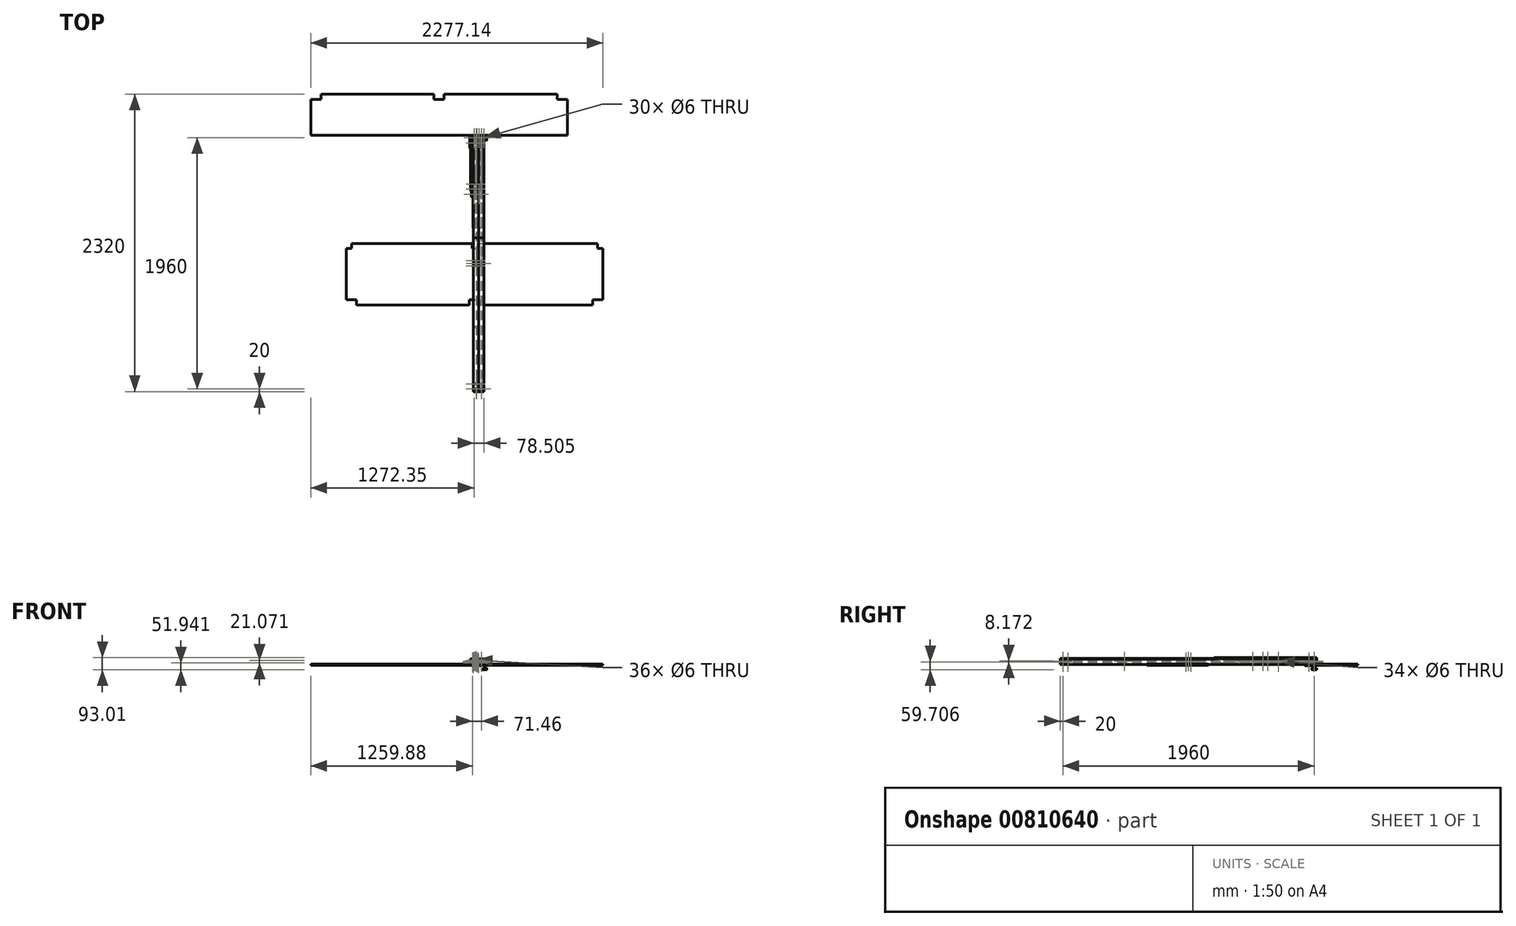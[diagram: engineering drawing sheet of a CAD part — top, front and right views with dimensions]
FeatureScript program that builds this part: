
annotation { "Feature Type Name" : "Feature", "Feature Type Description" : "" }
export const myFeature = defineFeature(function(context is Context, id is Id, definition is map)
    precondition{}
    {
        {
            var Q0;
            Q0=qCreatedBy(makeId("Front.planeOp"),FACE);
            var sketch = newSketch(context, id + "F0", { "sketchPlane" : qUnion([Q0])});
            skLineSegment(sketch, "E0.bottom", {"start": v(-48.85, 47.04) * mm, "end": v(31.15, 47.04) * mm});
            skLineSegment(sketch, "E0.top", {"start": v(-48.85, 7.04) * mm, "end": v(31.15, 7.04) * mm});
            skLineSegment(sketch, "E0.left", {"start": v(-48.85, 47.04) * mm, "end": v(-48.85, 7.04) * mm});
            skLineSegment(sketch, "E0.right", {"start": v(31.15, 47.04) * mm, "end": v(31.15, 7.04) * mm});
            skSolve(sketch);
        }
        {
            var Q0;
            Q0=makeQuery(id+"F0.imprint","IMPRINT",FACE,{"disambiguationData":[TD([[makeQuery(id+"F0.imprint","IMPRINT",EDGE,{"derivedFrom":sQuery(id+"F0.wireOp",EDGE,"E0.bottom")}),-1.0]])]});
            extrude(context, id + "F1", {"entities" : qUnion([Q0]), "depth" : 2000 * mm, "offsetDistance" : 25 * mm});
        }
        {
            var Q0;
            Q0=makeQuery(id+"F1.opExtrude","CAP_FACE",FACE,{"disambiguationData":[OSD([sQuery(id+"F0.wireOp",EDGE,"E0.bottom"),sQuery(id+"F0.wireOp",EDGE,"E0.top"),sQuery(id+"F0.wireOp",EDGE,"E0.left"),sQuery(id+"F0.wireOp",EDGE,"E0.right")])],"isStart":false});
            var sketch = newSketch(context, id + "F2", { "sketchPlane" : qUnion([Q0])});
            skPoint(sketch, "E1", {"position": v(-28.85, 27.04) * mm});
            skPoint(sketch, "E2", {"position": v(11.15, 27.04) * mm});
            skSolve(sketch);
        }
        {
            var Q0;
            Q0=makeQuery(id+"F1.opExtrude","SWEPT_EDGE",EDGE,{"disambiguationData":[OSD([sQuery(id+"F0.wireOp",EDGE,"E0.bottom"),sQuery(id+"F0.wireOp",EDGE,"E0.left")])]});
            var Q1;
            Q1=makeQuery(id+"F1.opExtrude","SWEPT_EDGE",EDGE,{"disambiguationData":[OSD([sQuery(id+"F0.wireOp",EDGE,"E0.bottom"),sQuery(id+"F0.wireOp",EDGE,"E0.right")])]});
            var Q2;
            Q2=makeQuery(id+"F1.opExtrude","SWEPT_EDGE",EDGE,{"disambiguationData":[OSD([sQuery(id+"F0.wireOp",EDGE,"E0.top"),sQuery(id+"F0.wireOp",EDGE,"E0.right")])]});
            var Q3;
            Q3=makeQuery(id+"F1.opExtrude","SWEPT_EDGE",EDGE,{"disambiguationData":[OSD([sQuery(id+"F0.wireOp",EDGE,"E0.top"),sQuery(id+"F0.wireOp",EDGE,"E0.left")])]});
            fillet(context, id + "F3", {"entities" : qUnion([Q0, Q1, Q2, Q3]), "radius" : 5 * mm, "tangentPropagation" : true, "allowEdgeOverflow" : false});
        }
        {
            var Q0;
            Q0=makeQuery(id+"F1.opExtrude","SWEPT_FACE",FACE,{"disambiguationData":[OSD([sQuery(id+"F0.wireOp",EDGE,"E0.left")])]});
            var sketch = newSketch(context, id + "F4", { "sketchPlane" : qUnion([Q0])});
            skPoint(sketch, "E3", {"position": v(20, 27.04) * mm});
            skPoint(sketch, "E4", {"position": v(60, 27.04) * mm});
            skPoint(sketch, "E5", {"position": v(1000, 27.04) * mm});
            skPoint(sketch, "E6", {"position": v(1020, 27.04) * mm});
            skPoint(sketch, "E7", {"position": v(980, 27.04) * mm});
            skPoint(sketch, "E8", {"position": v(1980, 27.04) * mm});
            skPoint(sketch, "E9", {"position": v(1940, 27.04) * mm});
            skSolve(sketch);
        }
        {
            var Q0;
            Q0=makeQuery(id+"F1.opExtrude","SWEPT_FACE",FACE,{"disambiguationData":[OSD([sQuery(id+"F0.wireOp",EDGE,"E0.top")])]});
            var sketch = newSketch(context, id + "F5", { "sketchPlane" : qUnion([Q0])});
            skPoint(sketch, "E10", {"position": v(-28.85, 1980) * mm});
            skPoint(sketch, "E11", {"position": v(11.15, 1980) * mm});
            skPoint(sketch, "E12", {"position": v(-28.85, 1000) * mm});
            skPoint(sketch, "E12.positionSnap0", {"position": v(-43.85, 1000) * mm});
            skPoint(sketch, "E13", {"position": v(11.15, 1000) * mm});
            skPoint(sketch, "E14", {"position": v(-28.85, 20) * mm});
            skPoint(sketch, "E15", {"position": v(11.15, 20) * mm});
            skSolve(sketch);
        }
        {
            var Q0;
            Q0=sQuery(id+"F5.wireOp",VERTEX,"E15");
            var Q1;
            Q1=sQuery(id+"F5.wireOp",VERTEX,"E14");
            var Q2;
            Q2=sQuery(id+"F4.wireOp",VERTEX,"E3");
            var Q3;
            Q3=sQuery(id+"F4.wireOp",VERTEX,"E4");
            var Q4;
            Q4=sQuery(id+"F4.wireOp",VERTEX,"E6");
            var Q5;
            Q5=sQuery(id+"F4.wireOp",VERTEX,"E7");
            var Q6;
            Q6=sQuery(id+"F5.wireOp",VERTEX,"E12");
            var Q7;
            Q7=sQuery(id+"F5.wireOp",VERTEX,"E13");
            var Q8;
            Q8=sQuery(id+"F4.wireOp",VERTEX,"E9");
            var Q9;
            Q9=sQuery(id+"F4.wireOp",VERTEX,"E8");
            var Q10;
            Q10=sQuery(id+"F5.wireOp",VERTEX,"E10");
            var Q11;
            Q11=sQuery(id+"F5.wireOp",VERTEX,"E11");
            var Q12;
            Q12=sQuery(id+"F2.wireOp",VERTEX,"E1");
            var Q13;
            Q13=sQuery(id+"F2.wireOp",VERTEX,"E2");
            var Q14;
            Q14=makeQuery(id+"F1.opExtrude","SWEPT_BODY",BODY,{"disambiguationData":[OSD([sQuery(id+"F0.wireOp",EDGE,"E0.bottom"),sQuery(id+"F0.wireOp",EDGE,"E0.top"),sQuery(id+"F0.wireOp",EDGE,"E0.left"),sQuery(id+"F0.wireOp",EDGE,"E0.right")])]});
            hole(context, id + "F6", {"style" : HoleStyle.SIMPLE, "endStyle" : HoleEndStyle.THROUGH, "holeDiameter" : 6 * mm, "majorDiameter" : 5 * mm, "isTappedThrough" : true, "tappedDepth" : 12 * mm, "tapClearance" : 3, "locations" : qUnion([Q0, Q1, Q2, Q3, Q4, Q5, Q6, Q7, Q8, Q9, Q10, Q11, Q12, Q13]), "scope" : qUnion([Q14])});
        }
        {
            var Q0;
            Q0=qCreatedBy(makeId("Front.planeOp"),FACE);
            var sketch = newSketch(context, id + "F7", { "sketchPlane" : qUnion([Q0])});
            skLineSegment(sketch, "E16.bottom", {"start": v(-49.88, 49.92) * mm, "end": v(30.12, 49.92) * mm});
            skLineSegment(sketch, "E16.top", {"start": v(-49.88, 9.08) * mm, "end": v(30.12, 9.08) * mm});
            skLineSegment(sketch, "E16.left", {"start": v(-49.88, 49.92) * mm, "end": v(-49.88, 9.08) * mm});
            skLineSegment(sketch, "E16.right", {"start": v(30.12, 49.92) * mm, "end": v(30.12, 9.08) * mm});
            skSolve(sketch);
        }
        {
            var Q0;
            Q0=makeQuery(id+"F7.imprint","IMPRINT",FACE,{"disambiguationData":[TD([[makeQuery(id+"F7.imprint","IMPRINT",EDGE,{"derivedFrom":sQuery(id+"F7.wireOp",EDGE,"E16.bottom")}),-1.0]])]});
            extrude(context, id + "F8", {"entities" : qUnion([Q0]), "depth" : 720 * mm, "offsetDistance" : 25 * mm});
        }
        {
            var Q0;
            Q0=makeQuery(id+"F8.opExtrude","CAP_FACE",FACE,{"disambiguationData":[OSD([sQuery(id+"F7.wireOp",EDGE,"E16.bottom"),sQuery(id+"F7.wireOp",EDGE,"E16.top"),sQuery(id+"F7.wireOp",EDGE,"E16.left"),sQuery(id+"F7.wireOp",EDGE,"E16.right")])],"isStart":false});
            var sketch = newSketch(context, id + "F9", { "sketchPlane" : qUnion([Q0])});
            skPoint(sketch, "E17", {"position": v(-29.88, 29.92) * mm});
            skPoint(sketch, "E18", {"position": v(10.12, 29.92) * mm});
            skSolve(sketch);
        }
        {
            var Q0;
            Q0=makeQuery(id+"F8.opExtrude","SWEPT_EDGE",EDGE,{"disambiguationData":[OSD([sQuery(id+"F7.wireOp",EDGE,"E16.bottom"),sQuery(id+"F7.wireOp",EDGE,"E16.left")])]});
            var Q1;
            Q1=makeQuery(id+"F8.opExtrude","SWEPT_EDGE",EDGE,{"disambiguationData":[OSD([sQuery(id+"F7.wireOp",EDGE,"E16.bottom"),sQuery(id+"F7.wireOp",EDGE,"E16.right")])]});
            var Q2;
            Q2=makeQuery(id+"F8.opExtrude","SWEPT_EDGE",EDGE,{"disambiguationData":[OSD([sQuery(id+"F7.wireOp",EDGE,"E16.top"),sQuery(id+"F7.wireOp",EDGE,"E16.right")])]});
            var Q3;
            Q3=makeQuery(id+"F8.opExtrude","SWEPT_EDGE",EDGE,{"disambiguationData":[OSD([sQuery(id+"F7.wireOp",EDGE,"E16.top"),sQuery(id+"F7.wireOp",EDGE,"E16.left")])]});
            fillet(context, id + "F10", {"entities" : qUnion([Q0, Q1, Q2, Q3]), "radius" : 5 * mm, "tangentPropagation" : true, "allowEdgeOverflow" : false});
        }
        {
            var Q0;
            Q0=sQuery(id+"F9.wireOp",VERTEX,"E17");
            var Q1;
            Q1=sQuery(id+"F9.wireOp",VERTEX,"E18");
            var Q2;
            Q2=makeQuery(id+"F8.opExtrude","SWEPT_BODY",BODY,{"disambiguationData":[OSD([sQuery(id+"F7.wireOp",EDGE,"E16.bottom"),sQuery(id+"F7.wireOp",EDGE,"E16.top"),sQuery(id+"F7.wireOp",EDGE,"E16.left"),sQuery(id+"F7.wireOp",EDGE,"E16.right")])]});
            hole(context, id + "F11", {"style" : HoleStyle.SIMPLE, "endStyle" : HoleEndStyle.THROUGH, "holeDiameter" : 6 * mm, "majorDiameter" : 5 * mm, "isTappedThrough" : true, "tappedDepth" : 12 * mm, "tapClearance" : 3, "locations" : qUnion([Q0, Q1]), "scope" : qUnion([Q2])});
        }
        {
            var Q0;
            Q0=qCreatedBy(makeId("Front.planeOp"),FACE);
            var sketch = newSketch(context, id + "F12", { "sketchPlane" : qUnion([Q0])});
            skLineSegment(sketch, "E19.bottom", {"start": v(-50.66, 52.94) * mm, "end": v(29.34, 52.94) * mm});
            skLineSegment(sketch, "E19.top", {"start": v(-50.66, 12.94) * mm, "end": v(29.34, 12.94) * mm});
            skLineSegment(sketch, "E19.left", {"start": v(-50.66, 52.94) * mm, "end": v(-50.66, 12.94) * mm});
            skLineSegment(sketch, "E19.right", {"start": v(29.34, 52.94) * mm, "end": v(29.34, 12.94) * mm});
            skSolve(sketch);
        }
        {
            var Q0;
            Q0=makeQuery(id+"F12.imprint","IMPRINT",FACE,{"disambiguationData":[TD([[makeQuery(id+"F12.imprint","IMPRINT",EDGE,{"derivedFrom":sQuery(id+"F12.wireOp",EDGE,"E19.bottom")}),-1.0]])]});
            extrude(context, id + "F13", {"entities" : qUnion([Q0]), "depth" : 800 * mm, "offsetDistance" : 25 * mm});
        }
        {
            var Q0;
            Q0=makeQuery(id+"F13.opExtrude","SWEPT_EDGE",EDGE,{"disambiguationData":[OSD([sQuery(id+"F12.wireOp",EDGE,"E19.bottom"),sQuery(id+"F12.wireOp",EDGE,"E19.left")])]});
            var Q1;
            Q1=makeQuery(id+"F13.opExtrude","SWEPT_EDGE",EDGE,{"disambiguationData":[OSD([sQuery(id+"F12.wireOp",EDGE,"E19.bottom"),sQuery(id+"F12.wireOp",EDGE,"E19.right")])]});
            var Q2;
            Q2=makeQuery(id+"F13.opExtrude","SWEPT_EDGE",EDGE,{"disambiguationData":[OSD([sQuery(id+"F12.wireOp",EDGE,"E19.top"),sQuery(id+"F12.wireOp",EDGE,"E19.left")])]});
            var Q3;
            Q3=makeQuery(id+"F13.opExtrude","SWEPT_EDGE",EDGE,{"disambiguationData":[OSD([sQuery(id+"F12.wireOp",EDGE,"E19.top"),sQuery(id+"F12.wireOp",EDGE,"E19.right")])]});
            fillet(context, id + "F14", {"entities" : qUnion([Q0, Q1, Q2, Q3]), "radius" : 5 * mm, "tangentPropagation" : true, "allowEdgeOverflow" : false});
        }
        {
            var Q0;
            Q0=makeQuery(id+"F13.opExtrude","CAP_FACE",FACE,{"disambiguationData":[OSD([sQuery(id+"F12.wireOp",EDGE,"E19.bottom"),sQuery(id+"F12.wireOp",EDGE,"E19.top"),sQuery(id+"F12.wireOp",EDGE,"E19.left"),sQuery(id+"F12.wireOp",EDGE,"E19.right")])],"isStart":false});
            var sketch = newSketch(context, id + "F15", { "sketchPlane" : qUnion([Q0])});
            skPoint(sketch, "E20", {"position": v(-30.66, 32.94) * mm});
            skPoint(sketch, "E20.positionSnap0", {"position": v(-50.66, 32.94) * mm});
            skPoint(sketch, "E21", {"position": v(9.34, 32.94) * mm});
            skSolve(sketch);
        }
        {
            var Q0;
            Q0=makeQuery(id+"F13.opExtrude","SWEPT_FACE",FACE,{"disambiguationData":[OSD([sQuery(id+"F12.wireOp",EDGE,"E19.left")])]});
            var sketch = newSketch(context, id + "F16", { "sketchPlane" : qUnion([Q0])});
            skPoint(sketch, "E22", {"position": v(400, 32.94) * mm});
            skPoint(sketch, "E23", {"position": v(420, 32.94) * mm});
            skPoint(sketch, "E24", {"position": v(380, 32.94) * mm});
            skSolve(sketch);
        }
        {
            var Q0;
            Q0=sQuery(id+"F16.wireOp",VERTEX,"E24");
            var Q1;
            Q1=sQuery(id+"F16.wireOp",VERTEX,"E23");
            var Q2;
            Q2=sQuery(id+"F15.wireOp",VERTEX,"E20");
            var Q3;
            Q3=sQuery(id+"F15.wireOp",VERTEX,"E21");
            var Q4;
            Q4=makeQuery(id+"F13.opExtrude","SWEPT_BODY",BODY,{"disambiguationData":[OSD([sQuery(id+"F12.wireOp",EDGE,"E19.bottom"),sQuery(id+"F12.wireOp",EDGE,"E19.top"),sQuery(id+"F12.wireOp",EDGE,"E19.left"),sQuery(id+"F12.wireOp",EDGE,"E19.right")])]});
            hole(context, id + "F17", {"style" : HoleStyle.SIMPLE, "endStyle" : HoleEndStyle.THROUGH, "holeDiameter" : 6 * mm, "majorDiameter" : 5 * mm, "isTappedThrough" : true, "tappedDepth" : 12 * mm, "tapClearance" : 3, "locations" : qUnion([Q0, Q1, Q2, Q3]), "scope" : qUnion([Q4])});
        }
        {
            var Q0;
            Q0=qCreatedBy(makeId("Front.planeOp"),FACE);
            var sketch = newSketch(context, id + "F18", { "sketchPlane" : qUnion([Q0])});
            skLineSegment(sketch, "E25.bottom", {"start": v(-51.7, 60.34) * mm, "end": v(-11.7, 60.34) * mm});
            skLineSegment(sketch, "E25.top", {"start": v(-51.7, 20.34) * mm, "end": v(-11.7, 20.34) * mm});
            skLineSegment(sketch, "E25.left", {"start": v(-51.7, 60.34) * mm, "end": v(-51.7, 20.34) * mm});
            skLineSegment(sketch, "E25.right", {"start": v(-11.7, 60.34) * mm, "end": v(-11.7, 20.34) * mm});
            skSolve(sketch);
        }
        {
            var Q0;
            Q0=makeQuery(id+"F18.imprint","IMPRINT",FACE,{"disambiguationData":[TD([[makeQuery(id+"F18.imprint","IMPRINT",EDGE,{"derivedFrom":sQuery(id+"F18.wireOp",EDGE,"E25.bottom")}),-1.0]])]});
            extrude(context, id + "F19", {"entities" : qUnion([Q0]), "depth" : 800 * mm, "offsetDistance" : 25 * mm});
        }
        {
            var Q0;
            Q0=makeQuery(id+"F19.opExtrude","SWEPT_EDGE",EDGE,{"disambiguationData":[OSD([sQuery(id+"F18.wireOp",EDGE,"E25.bottom"),sQuery(id+"F18.wireOp",EDGE,"E25.left")])]});
            var Q1;
            Q1=makeQuery(id+"F19.opExtrude","SWEPT_EDGE",EDGE,{"disambiguationData":[OSD([sQuery(id+"F18.wireOp",EDGE,"E25.bottom"),sQuery(id+"F18.wireOp",EDGE,"E25.right")])]});
            var Q2;
            Q2=makeQuery(id+"F19.opExtrude","SWEPT_EDGE",EDGE,{"disambiguationData":[OSD([sQuery(id+"F18.wireOp",EDGE,"E25.top"),sQuery(id+"F18.wireOp",EDGE,"E25.right")])]});
            var Q3;
            Q3=makeQuery(id+"F19.opExtrude","SWEPT_EDGE",EDGE,{"disambiguationData":[OSD([sQuery(id+"F18.wireOp",EDGE,"E25.top"),sQuery(id+"F18.wireOp",EDGE,"E25.left")])]});
            fillet(context, id + "F20", {"entities" : qUnion([Q0, Q1, Q2, Q3]), "radius" : 5 * mm, "tangentPropagation" : true, "allowEdgeOverflow" : false});
        }
        {
            var Q0;
            Q0=makeQuery(id+"F19.opExtrude","CAP_FACE",FACE,{"disambiguationData":[OSD([sQuery(id+"F18.wireOp",EDGE,"E25.bottom"),sQuery(id+"F18.wireOp",EDGE,"E25.top"),sQuery(id+"F18.wireOp",EDGE,"E25.left"),sQuery(id+"F18.wireOp",EDGE,"E25.right")])],"isStart":false});
            var sketch = newSketch(context, id + "F21", { "sketchPlane" : qUnion([Q0])});
            skPoint(sketch, "E26", {"position": v(-31.7, 40.34) * mm});
            skPoint(sketch, "E26.positionSnap0", {"position": v(-51.7, 40.34) * mm});
            skPoint(sketch, "E26.positionSnap1", {"position": v(-31.7, 60.34) * mm});
            skSolve(sketch);
        }
        {
            var Q0;
            Q0=makeQuery(id+"F19.opExtrude","SWEPT_FACE",FACE,{"disambiguationData":[OSD([sQuery(id+"F18.wireOp",EDGE,"E25.bottom")])]});
            var sketch = newSketch(context, id + "F22", { "sketchPlane" : qUnion([Q0])});
            skPoint(sketch, "E27", {"position": v(-31.7, -400) * mm});
            skPoint(sketch, "E28", {"position": v(-31.7, -380) * mm});
            skPoint(sketch, "E29", {"position": v(-31.7, -420) * mm});
            skSolve(sketch);
        }
        {
            var Q0;
            Q0=sQuery(id+"F22.wireOp",VERTEX,"E28");
            var Q1;
            Q1=sQuery(id+"F22.wireOp",VERTEX,"E29");
            var Q2;
            Q2=sQuery(id+"F21.wireOp",VERTEX,"E26");
            var Q3;
            Q3=makeQuery(id+"F19.opExtrude","SWEPT_BODY",BODY,{"disambiguationData":[OSD([sQuery(id+"F18.wireOp",EDGE,"E25.bottom"),sQuery(id+"F18.wireOp",EDGE,"E25.top"),sQuery(id+"F18.wireOp",EDGE,"E25.left"),sQuery(id+"F18.wireOp",EDGE,"E25.right")])]});
            hole(context, id + "F23", {"style" : HoleStyle.SIMPLE, "endStyle" : HoleEndStyle.THROUGH, "holeDiameter" : 6 * mm, "majorDiameter" : 5 * mm, "isTappedThrough" : true, "tappedDepth" : 12 * mm, "tapClearance" : 3, "locations" : qUnion([Q0, Q1, Q2]), "scope" : qUnion([Q3])});
        }
        {
            var Q0;
            Q0=qCreatedBy(makeId("Front.planeOp"),FACE);
            var sketch = newSketch(context, id + "F24", { "sketchPlane" : qUnion([Q0])});
            skLineSegment(sketch, "E30.bottom", {"start": v(-51.72, 54) * mm, "end": v(-11.72, 54) * mm});
            skLineSegment(sketch, "E30.top", {"start": v(-51.72, 14) * mm, "end": v(-11.72, 14) * mm});
            skLineSegment(sketch, "E30.left", {"start": v(-51.72, 54) * mm, "end": v(-51.72, 14) * mm});
            skLineSegment(sketch, "E30.right", {"start": v(-11.72, 54) * mm, "end": v(-11.72, 14) * mm});
            skSolve(sketch);
        }
        {
            var Q0;
            Q0=makeQuery(id+"F24.imprint","IMPRINT",FACE,{"disambiguationData":[TD([[makeQuery(id+"F24.imprint","IMPRINT",EDGE,{"derivedFrom":sQuery(id+"F24.wireOp",EDGE,"E30.bottom")}),-1.0]])]});
            extrude(context, id + "F25", {"entities" : qUnion([Q0]), "depth" : 2000 * mm, "offsetDistance" : 25 * mm});
        }
        {
            var Q0;
            Q0=makeQuery(id+"F25.opExtrude","SWEPT_EDGE",EDGE,{"disambiguationData":[OSD([sQuery(id+"F24.wireOp",EDGE,"E30.bottom"),sQuery(id+"F24.wireOp",EDGE,"E30.left")])]});
            var Q1;
            Q1=makeQuery(id+"F25.opExtrude","SWEPT_EDGE",EDGE,{"disambiguationData":[OSD([sQuery(id+"F24.wireOp",EDGE,"E30.bottom"),sQuery(id+"F24.wireOp",EDGE,"E30.right")])]});
            var Q2;
            Q2=makeQuery(id+"F25.opExtrude","SWEPT_EDGE",EDGE,{"disambiguationData":[OSD([sQuery(id+"F24.wireOp",EDGE,"E30.top"),sQuery(id+"F24.wireOp",EDGE,"E30.right")])]});
            var Q3;
            Q3=makeQuery(id+"F25.opExtrude","SWEPT_EDGE",EDGE,{"disambiguationData":[OSD([sQuery(id+"F24.wireOp",EDGE,"E30.top"),sQuery(id+"F24.wireOp",EDGE,"E30.left")])]});
            fillet(context, id + "F26", {"entities" : qUnion([Q0, Q1, Q2, Q3]), "radius" : 5 * mm, "tangentPropagation" : true, "allowEdgeOverflow" : false});
        }
        {
            var Q0;
            Q0=makeQuery(id+"F25.opExtrude","SWEPT_FACE",FACE,{"disambiguationData":[OSD([sQuery(id+"F24.wireOp",EDGE,"E30.left")])]});
            var sketch = newSketch(context, id + "F27", { "sketchPlane" : qUnion([Q0])});
            skPoint(sketch, "E31", {"position": v(20, 34) * mm});
            skPoint(sketch, "E31.positionSnap0", {"position": v(0, 34) * mm});
            skPoint(sketch, "E32", {"position": v(1000, 34) * mm});
            skPoint(sketch, "E33", {"position": v(500, 34) * mm});
            skPoint(sketch, "E34", {"position": v(1500, 34) * mm});
            skPoint(sketch, "E35", {"position": v(1980, 34) * mm});
            skSolve(sketch);
        }
        {
            var Q0;
            Q0=makeQuery(id+"F25.opExtrude","SWEPT_FACE",FACE,{"disambiguationData":[OSD([sQuery(id+"F24.wireOp",EDGE,"E30.bottom")])]});
            var sketch = newSketch(context, id + "F28", { "sketchPlane" : qUnion([Q0])});
            skPoint(sketch, "E36", {"position": v(-31.72, -1980) * mm});
            skPoint(sketch, "E36.positionSnap0", {"position": v(-31.72, -2000) * mm});
            skPoint(sketch, "E37", {"position": v(-31.72, -1940) * mm});
            skPoint(sketch, "E38", {"position": v(-31.72, -1000) * mm});
            skPoint(sketch, "E39", {"position": v(-31.72, -1020) * mm});
            skPoint(sketch, "E40", {"position": v(-31.72, -980) * mm});
            skPoint(sketch, "E41", {"position": v(-31.72, -20) * mm});
            skPoint(sketch, "E42", {"position": v(-31.72, -60) * mm});
            skSolve(sketch);
        }
        {
            var Q0;
            Q0=sQuery(id+"F28.wireOp",VERTEX,"E36");
            var Q1;
            Q1=sQuery(id+"F28.wireOp",VERTEX,"E37");
            var Q2;
            Q2=sQuery(id+"F28.wireOp",VERTEX,"E39");
            var Q3;
            Q3=sQuery(id+"F28.wireOp",VERTEX,"E40");
            var Q4;
            Q4=sQuery(id+"F27.wireOp",VERTEX,"E34");
            var Q5;
            Q5=sQuery(id+"F27.wireOp",VERTEX,"E35");
            var Q6;
            Q6=sQuery(id+"F27.wireOp",VERTEX,"E32");
            var Q7;
            Q7=sQuery(id+"F27.wireOp",VERTEX,"E33");
            var Q8;
            Q8=sQuery(id+"F28.wireOp",VERTEX,"E42");
            var Q9;
            Q9=sQuery(id+"F28.wireOp",VERTEX,"E41");
            var Q10;
            Q10=sQuery(id+"F27.wireOp",VERTEX,"E31");
            var Q11;
            Q11=makeQuery(id+"F25.opExtrude","SWEPT_BODY",BODY,{"disambiguationData":[OSD([sQuery(id+"F24.wireOp",EDGE,"E30.bottom"),sQuery(id+"F24.wireOp",EDGE,"E30.top"),sQuery(id+"F24.wireOp",EDGE,"E30.left"),sQuery(id+"F24.wireOp",EDGE,"E30.right")])]});
            hole(context, id + "F29", {"style" : HoleStyle.SIMPLE, "endStyle" : HoleEndStyle.THROUGH, "holeDiameter" : 6 * mm, "majorDiameter" : 5 * mm, "isTappedThrough" : true, "tappedDepth" : 12 * mm, "tapClearance" : 3, "locations" : qUnion([Q0, Q1, Q2, Q3, Q4, Q5, Q6, Q7, Q8, Q9, Q10]), "scope" : qUnion([Q11])});
        }
        {
            var Q0;
            Q0=qCreatedBy(makeId("Front.planeOp"),FACE);
            var sketch = newSketch(context, id + "F30", { "sketchPlane" : qUnion([Q0])});
            skLineSegment(sketch, "E43.bottom", {"start": v(-55.62, 55.2) * mm, "end": v(-15.62, 55.2) * mm});
            skLineSegment(sketch, "E43.top", {"start": v(-55.62, 15.2) * mm, "end": v(-15.62, 15.2) * mm});
            skLineSegment(sketch, "E43.left", {"start": v(-55.62, 55.2) * mm, "end": v(-55.62, 15.2) * mm});
            skLineSegment(sketch, "E43.right", {"start": v(-15.62, 55.2) * mm, "end": v(-15.62, 15.2) * mm});
            skSolve(sketch);
        }
        {
            var Q0;
            Q0=makeQuery(id+"F30.imprint","IMPRINT",FACE,{"disambiguationData":[TD([[makeQuery(id+"F30.imprint","IMPRINT",EDGE,{"derivedFrom":sQuery(id+"F30.wireOp",EDGE,"E43.bottom")}),-1.0]])]});
            extrude(context, id + "F31", {"entities" : qUnion([Q0]), "depth" : 720 * mm, "offsetDistance" : 25 * mm});
        }
        {
            var Q0;
            Q0=makeQuery(id+"F31.opExtrude","SWEPT_EDGE",EDGE,{"disambiguationData":[OSD([sQuery(id+"F30.wireOp",EDGE,"E43.bottom"),sQuery(id+"F30.wireOp",EDGE,"E43.left")])]});
            var Q1;
            Q1=makeQuery(id+"F31.opExtrude","SWEPT_EDGE",EDGE,{"disambiguationData":[OSD([sQuery(id+"F30.wireOp",EDGE,"E43.bottom"),sQuery(id+"F30.wireOp",EDGE,"E43.right")])]});
            var Q2;
            Q2=makeQuery(id+"F31.opExtrude","SWEPT_EDGE",EDGE,{"disambiguationData":[OSD([sQuery(id+"F30.wireOp",EDGE,"E43.top"),sQuery(id+"F30.wireOp",EDGE,"E43.right")])]});
            var Q3;
            Q3=makeQuery(id+"F31.opExtrude","SWEPT_EDGE",EDGE,{"disambiguationData":[OSD([sQuery(id+"F30.wireOp",EDGE,"E43.top"),sQuery(id+"F30.wireOp",EDGE,"E43.left")])]});
            fillet(context, id + "F32", {"entities" : qUnion([Q0, Q1, Q2, Q3]), "radius" : 5 * mm, "tangentPropagation" : true, "allowEdgeOverflow" : false});
        }
        {
            var Q0;
            Q0=makeQuery(id+"F31.opExtrude","CAP_FACE",FACE,{"disambiguationData":[OSD([sQuery(id+"F30.wireOp",EDGE,"E43.bottom"),sQuery(id+"F30.wireOp",EDGE,"E43.top"),sQuery(id+"F30.wireOp",EDGE,"E43.left"),sQuery(id+"F30.wireOp",EDGE,"E43.right")])],"isStart":false});
            var sketch = newSketch(context, id + "F33", { "sketchPlane" : qUnion([Q0])});
            skPoint(sketch, "E44", {"position": v(-35.62, 35.2) * mm});
            skPoint(sketch, "E44.positionSnap0", {"position": v(-55.62, 35.2) * mm});
            skPoint(sketch, "E44.positionSnap1", {"position": v(-35.62, 55.2) * mm});
            skSolve(sketch);
        }
        {
            var Q0;
            Q0=sQuery(id+"F33.wireOp",VERTEX,"E44");
            var Q1;
            Q1=makeQuery(id+"F31.opExtrude","SWEPT_BODY",BODY,{"disambiguationData":[OSD([sQuery(id+"F30.wireOp",EDGE,"E43.bottom"),sQuery(id+"F30.wireOp",EDGE,"E43.top"),sQuery(id+"F30.wireOp",EDGE,"E43.left"),sQuery(id+"F30.wireOp",EDGE,"E43.right")])]});
            hole(context, id + "F34", {"style" : HoleStyle.SIMPLE, "endStyle" : HoleEndStyle.THROUGH, "holeDiameter" : 6 * mm, "majorDiameter" : 5 * mm, "isTappedThrough" : true, "tappedDepth" : 12 * mm, "tapClearance" : 3, "locations" : qUnion([Q0]), "scope" : qUnion([Q1])});
        }
        {
            var Q0;
            Q0=makeQuery(id+"F8.opExtrude","SWEPT_FACE",FACE,{"disambiguationData":[OSD([sQuery(id+"F7.wireOp",EDGE,"E16.right")])]});
            var sketch = newSketch(context, id + "F35", { "sketchPlane" : qUnion([Q0])});
            skPoint(sketch, "E45", {"position": v(-300, 29.08) * mm});
            skSolve(sketch);
        }
        {
            var Q0;
            Q0=sQuery(id+"F35.wireOp",VERTEX,"E45");
            var Q1;
            Q1=makeQuery(id+"F8.opExtrude","SWEPT_BODY",BODY,{"disambiguationData":[OSD([sQuery(id+"F7.wireOp",EDGE,"E16.bottom"),sQuery(id+"F7.wireOp",EDGE,"E16.top"),sQuery(id+"F7.wireOp",EDGE,"E16.left"),sQuery(id+"F7.wireOp",EDGE,"E16.right")])]});
            hole(context, id + "F36", {"style" : HoleStyle.SIMPLE, "endStyle" : HoleEndStyle.THROUGH, "holeDiameter" : 6 * mm, "majorDiameter" : 5 * mm, "isTappedThrough" : true, "tappedDepth" : 12 * mm, "tapClearance" : 3, "locations" : qUnion([Q0]), "scope" : qUnion([Q1])});
        }
        {
            var Q0;
            Q0=makeQuery(id+"F31.opExtrude","SWEPT_FACE",FACE,{"disambiguationData":[OSD([sQuery(id+"F30.wireOp",EDGE,"E43.right")])]});
            var sketch = newSketch(context, id + "F37", { "sketchPlane" : qUnion([Q0])});
            skPoint(sketch, "E46", {"position": v(-300, 35.2) * mm});
            skSolve(sketch);
        }
        {
            var Q0;
            Q0=sQuery(id+"F37.wireOp",VERTEX,"E46");
            var Q1;
            Q1=makeQuery(id+"F31.opExtrude","SWEPT_BODY",BODY,{"disambiguationData":[OSD([sQuery(id+"F30.wireOp",EDGE,"E43.bottom"),sQuery(id+"F30.wireOp",EDGE,"E43.top"),sQuery(id+"F30.wireOp",EDGE,"E43.left"),sQuery(id+"F30.wireOp",EDGE,"E43.right")])]});
            hole(context, id + "F38", {"style" : HoleStyle.SIMPLE, "endStyle" : HoleEndStyle.THROUGH, "holeDiameter" : 6 * mm, "majorDiameter" : 5 * mm, "isTappedThrough" : true, "tappedDepth" : 12 * mm, "tapClearance" : 3, "locations" : qUnion([Q0]), "scope" : qUnion([Q1])});
        }
        {
            var Q0;
            Q0=qCreatedBy(makeId("Front.planeOp"),FACE);
            var sketch = newSketch(context, id + "F39", { "sketchPlane" : qUnion([Q0])});
            skLineSegment(sketch, "E47.bottom", {"start": v(-80.31, 44.3) * mm, "end": v(-0.31, 44.3) * mm});
            skLineSegment(sketch, "E47.top", {"start": v(-80.31, 4.3) * mm, "end": v(-0.31, 4.3) * mm});
            skLineSegment(sketch, "E47.left", {"start": v(-80.31, 44.3) * mm, "end": v(-80.31, 4.3) * mm});
            skLineSegment(sketch, "E47.right", {"start": v(-0.31, 44.3) * mm, "end": v(-0.31, 4.3) * mm});
            skSolve(sketch);
        }
        {
            var Q0;
            Q0=makeQuery(id+"F39.imprint","IMPRINT",FACE,{"disambiguationData":[TD([[makeQuery(id+"F39.imprint","IMPRINT",EDGE,{"derivedFrom":sQuery(id+"F39.wireOp",EDGE,"E47.bottom")}),-1.0]])]});
            extrude(context, id + "F40", {"entities" : qUnion([Q0]), "depth" : 100 * mm, "offsetDistance" : 25 * mm});
        }
        {
            var Q0;
            Q0=makeQuery(id+"F40.opExtrude","SWEPT_EDGE",EDGE,{"disambiguationData":[OSD([sQuery(id+"F39.wireOp",EDGE,"E47.bottom"),sQuery(id+"F39.wireOp",EDGE,"E47.left")])]});
            var Q1;
            Q1=makeQuery(id+"F40.opExtrude","SWEPT_EDGE",EDGE,{"disambiguationData":[OSD([sQuery(id+"F39.wireOp",EDGE,"E47.top"),sQuery(id+"F39.wireOp",EDGE,"E47.left")])]});
            var Q2;
            Q2=makeQuery(id+"F40.opExtrude","SWEPT_EDGE",EDGE,{"disambiguationData":[OSD([sQuery(id+"F39.wireOp",EDGE,"E47.bottom"),sQuery(id+"F39.wireOp",EDGE,"E47.right")])]});
            var Q3;
            Q3=makeQuery(id+"F40.opExtrude","SWEPT_EDGE",EDGE,{"disambiguationData":[OSD([sQuery(id+"F39.wireOp",EDGE,"E47.top"),sQuery(id+"F39.wireOp",EDGE,"E47.right")])]});
            fillet(context, id + "F41", {"entities" : qUnion([Q0, Q1, Q2, Q3]), "radius" : 5 * mm, "tangentPropagation" : true, "allowEdgeOverflow" : false});
        }
        {
            var Q0;
            Q0=makeQuery(id+"F40.opExtrude","CAP_FACE",FACE,{"disambiguationData":[OSD([sQuery(id+"F39.wireOp",EDGE,"E47.bottom"),sQuery(id+"F39.wireOp",EDGE,"E47.top"),sQuery(id+"F39.wireOp",EDGE,"E47.left"),sQuery(id+"F39.wireOp",EDGE,"E47.right")])],"isStart":false});
            var sketch = newSketch(context, id + "F42", { "sketchPlane" : qUnion([Q0])});
            skPoint(sketch, "E48", {"position": v(-60.31, 24.3) * mm});
            skPoint(sketch, "E48.positionSnap0", {"position": v(-80.31, 24.3) * mm});
            skPoint(sketch, "E49", {"position": v(-20.31, 24.3) * mm});
            skSolve(sketch);
        }
        {
            var Q0;
            Q0=sQuery(id+"F42.wireOp",VERTEX,"E48");
            var Q1;
            Q1=sQuery(id+"F42.wireOp",VERTEX,"E49");
            var Q2;
            Q2=makeQuery(id+"F40.opExtrude","SWEPT_BODY",BODY,{"disambiguationData":[OSD([sQuery(id+"F39.wireOp",EDGE,"E47.bottom"),sQuery(id+"F39.wireOp",EDGE,"E47.top"),sQuery(id+"F39.wireOp",EDGE,"E47.left"),sQuery(id+"F39.wireOp",EDGE,"E47.right")])]});
            hole(context, id + "F43", {"style" : HoleStyle.SIMPLE, "endStyle" : HoleEndStyle.THROUGH, "holeDiameter" : 6 * mm, "majorDiameter" : 5 * mm, "isTappedThrough" : true, "tappedDepth" : 12 * mm, "tapClearance" : 3, "locations" : qUnion([Q0, Q1]), "scope" : qUnion([Q2])});
        }
        {
            var Q0;
            Q0=qCreatedBy(makeId("Front.planeOp"),FACE);
            var sketch = newSketch(context, id + "F44", { "sketchPlane" : qUnion([Q0])});
            skLineSegment(sketch, "E50.bottom", {"start": v(-67.84, 51.91) * mm, "end": v(12.16, 51.91) * mm});
            skLineSegment(sketch, "E50.top", {"start": v(-67.84, 11.91) * mm, "end": v(12.16, 11.91) * mm});
            skLineSegment(sketch, "E50.left", {"start": v(-67.84, 51.91) * mm, "end": v(-67.84, 11.91) * mm});
            skLineSegment(sketch, "E50.right", {"start": v(12.16, 51.91) * mm, "end": v(12.16, 11.91) * mm});
            skSolve(sketch);
        }
        {
            var Q0;
            Q0=makeQuery(id+"F44.imprint","IMPRINT",FACE,{"disambiguationData":[TD([[makeQuery(id+"F44.imprint","IMPRINT",EDGE,{"derivedFrom":sQuery(id+"F44.wireOp",EDGE,"E50.bottom")}),-1.0]])]});
            extrude(context, id + "F45", {"entities" : qUnion([Q0]), "depth" : 480 * mm, "offsetDistance" : 25 * mm});
        }
        {
            var Q0;
            Q0=makeQuery(id+"F45.opExtrude","SWEPT_EDGE",EDGE,{"disambiguationData":[OSD([sQuery(id+"F44.wireOp",EDGE,"E50.bottom"),sQuery(id+"F44.wireOp",EDGE,"E50.left")])]});
            var Q1;
            Q1=makeQuery(id+"F45.opExtrude","SWEPT_EDGE",EDGE,{"disambiguationData":[OSD([sQuery(id+"F44.wireOp",EDGE,"E50.bottom"),sQuery(id+"F44.wireOp",EDGE,"E50.right")])]});
            var Q2;
            Q2=makeQuery(id+"F45.opExtrude","SWEPT_EDGE",EDGE,{"disambiguationData":[OSD([sQuery(id+"F44.wireOp",EDGE,"E50.top"),sQuery(id+"F44.wireOp",EDGE,"E50.right")])]});
            var Q3;
            Q3=makeQuery(id+"F45.opExtrude","SWEPT_EDGE",EDGE,{"disambiguationData":[OSD([sQuery(id+"F44.wireOp",EDGE,"E50.top"),sQuery(id+"F44.wireOp",EDGE,"E50.left")])]});
            fillet(context, id + "F46", {"entities" : qUnion([Q0, Q1, Q2, Q3]), "radius" : 5 * mm, "tangentPropagation" : true, "allowEdgeOverflow" : false});
        }
        {
            var Q0;
            Q0=makeQuery(id+"F45.opExtrude","SWEPT_FACE",FACE,{"disambiguationData":[OSD([sQuery(id+"F44.wireOp",EDGE,"E50.bottom")])]});
            var sketch = newSketch(context, id + "F47", { "sketchPlane" : qUnion([Q0])});
            skPoint(sketch, "E51", {"position": v(-47.84, -20) * mm});
            skPoint(sketch, "E52", {"position": v(-7.84, -20) * mm});
            skPoint(sketch, "E53", {"position": v(-47.84, -460) * mm});
            skPoint(sketch, "E54", {"position": v(-7.84, -460) * mm});
            skSolve(sketch);
        }
        {
            var Q0;
            Q0=sQuery(id+"F47.wireOp",VERTEX,"E51");
            var Q1;
            Q1=sQuery(id+"F47.wireOp",VERTEX,"E52");
            var Q2;
            Q2=sQuery(id+"F47.wireOp",VERTEX,"E54");
            var Q3;
            Q3=sQuery(id+"F47.wireOp",VERTEX,"E53");
            var Q4;
            Q4=makeQuery(id+"F45.opExtrude","SWEPT_BODY",BODY,{"disambiguationData":[OSD([sQuery(id+"F44.wireOp",EDGE,"E50.bottom"),sQuery(id+"F44.wireOp",EDGE,"E50.top"),sQuery(id+"F44.wireOp",EDGE,"E50.left"),sQuery(id+"F44.wireOp",EDGE,"E50.right")])]});
            hole(context, id + "F48", {"style" : HoleStyle.SIMPLE, "endStyle" : HoleEndStyle.THROUGH, "holeDiameter" : 6 * mm, "majorDiameter" : 5 * mm, "isTappedThrough" : true, "tappedDepth" : 12 * mm, "tapClearance" : 3, "locations" : qUnion([Q0, Q1, Q2, Q3]), "scope" : qUnion([Q4])});
        }
        {
            var Q0;
            Q0=qCreatedBy(makeId("Top.planeOp"),FACE);
            var sketch = newSketch(context, id + "F49", { "sketchPlane" : qUnion([Q0])});
            skLineSegment(sketch, "E55.bottom", {"start": v(-1003.05, -843.62) * mm, "end": v(-63.05, -843.62) * mm});
            skLineSegment(sketch, "E55.top", {"start": v(-962.92, -1323.62) * mm, "end": v(-83.05, -1323.62) * mm});
            skLineSegment(sketch, "E55.left", {"start": v(-1043.05, -883.76) * mm, "end": v(-1043.05, -1283.9) * mm});
            skLineSegment(sketch, "E55.right", {"start": v(956.95, -883.62) * mm, "end": v(956.95, -1283.62) * mm});
            skPoint(sketch, "E56", {"position": v(-1003.05, -883.62) * mm});
            skPoint(sketch, "E57", {"position": v(-963.05, -1283.62) * mm});
            skLineSegment(sketch, "E58", {"start": v(-1003.05, -883.62) * mm, "end": v(-1003.05, -843.62) * mm});
            skLineSegment(sketch, "E59", {"start": v(-1003.05, -843.62) * mm, "end": v(-1003.05, -883.62) * mm});
            skLineSegment(sketch, "E60", {"start": v(-1043.05, -883.76) * mm, "end": v(-1003.05, -883.62) * mm});
            skLineSegment(sketch, "E61", {"start": v(-963.05, -1283.62) * mm, "end": v(-1043.05, -1283.9) * mm});
            skLineSegment(sketch, "E62", {"start": v(-1043.05, -1283.9) * mm, "end": v(-963.05, -1283.62) * mm});
            skLineSegment(sketch, "E63", {"start": v(-963.05, -1283.62) * mm, "end": v(-962.92, -1323.62) * mm});
            skPoint(sketch, "E64", {"position": v(-63.05, -883.62) * mm});
            skPoint(sketch, "E65", {"position": v(-23.05, -883.62) * mm});
            skPoint(sketch, "E66", {"position": v(-83.05, -1283.62) * mm});
            skPoint(sketch, "E67", {"position": v(-3.05, -1283.62) * mm});
            skPoint(sketch, "E68", {"position": v(916.95, -883.62) * mm});
            skPoint(sketch, "E69", {"position": v(876.95, -1283.62) * mm});
            skLineSegment(sketch, "E70", {"start": v(916.95, -883.62) * mm, "end": v(916.95, -843.62) * mm});
            skLineSegment(sketch, "E71", {"start": v(916.95, -843.62) * mm, "end": v(916.95, -883.62) * mm});
            skLineSegment(sketch, "E72", {"start": v(916.95, -883.62) * mm, "end": v(956.95, -883.62) * mm});
            skLineSegment(sketch, "E73", {"start": v(956.95, -1283.62) * mm, "end": v(876.95, -1283.62) * mm});
            skPoint(sketch, "E73.startSnap0", {"position": v(956.95, -1083.62) * mm});
            skLineSegment(sketch, "E74", {"start": v(876.95, -1283.62) * mm, "end": v(876.95, -1323.62) * mm});
            skPoint(sketch, "E75.orphan", {"position": v(956.95, -843.62) * mm});
            skPoint(sketch, "E76.orphan", {"position": v(956.95, -1323.62) * mm});
            skLineSegment(sketch, "E77", {"start": v(-23.05, -843.62) * mm, "end": v(-23.05, -883.62) * mm});
            skLineSegment(sketch, "E78", {"start": v(-63.05, -883.62) * mm, "end": v(-23.05, -883.62) * mm});
            skLineSegment(sketch, "E79", {"start": v(-63.05, -883.62) * mm, "end": v(-63.05, -843.62) * mm});
            skLineSegment(sketch, "E80", {"start": v(-83.05, -1283.62) * mm, "end": v(-83.05, -1323.62) * mm});
            skLineSegment(sketch, "E81", {"start": v(-83.05, -1323.62) * mm, "end": v(-83.05, -1283.62) * mm});
            skLineSegment(sketch, "E82", {"start": v(-83.05, -1283.62) * mm, "end": v(-3.05, -1283.62) * mm});
            skLineSegment(sketch, "E83", {"start": v(-3.05, -1283.62) * mm, "end": v(-3.05, -1323.62) * mm});
            skLineSegment(sketch, "E84.trimOffspring", {"start": v(-3.05, -1323.62) * mm, "end": v(876.95, -1323.62) * mm});
            skLineSegment(sketch, "E85.trimOffspring", {"start": v(-23.05, -843.62) * mm, "end": v(916.95, -843.62) * mm});
            skSolve(sketch);
        }
        {
            var Q0;
            Q0=makeQuery(id+"F49.imprint","IMPRINT",FACE,{"disambiguationData":[TD([[makeQuery(id+"F49.imprint","IMPRINT",EDGE,{"derivedFrom":sQuery(id+"F49.wireOp",EDGE,"E55.bottom")}),-1.0]])]});
            extrude(context, id + "F50", {"entities" : qUnion([Q0]), "depth" : 12 * mm, "offsetDistance" : 25 * mm});
        }
        {
            var Q0;
            Q0=qCreatedBy(makeId("Top.planeOp"),FACE);
            var sketch = newSketch(context, id + "F51", { "sketchPlane" : qUnion([Q0])});
            skLineSegment(sketch, "E86.bottom", {"start": v(-1240.19, 320) * mm, "end": v(-360.19, 320) * mm});
            skLineSegment(sketch, "E86.top", {"start": v(-1320.19, 0) * mm, "end": v(679.81, 0) * mm});
            skLineSegment(sketch, "E86.left", {"start": v(-1320.19, 280) * mm, "end": v(-1320.19, 0) * mm});
            skLineSegment(sketch, "E86.right", {"start": v(679.81, 280) * mm, "end": v(679.81, 0) * mm});
            skPoint(sketch, "E87", {"position": v(599.81, 280) * mm});
            skPoint(sketch, "E88", {"position": v(-280.19, 280) * mm});
            skPoint(sketch, "E89", {"position": v(-360.19, 280) * mm});
            skPoint(sketch, "E90", {"position": v(-1240.19, 280) * mm});
            skLineSegment(sketch, "E91", {"start": v(-1240.19, 280) * mm, "end": v(-1240.19, 320) * mm});
            skLineSegment(sketch, "E92", {"start": v(-1240.19, 320) * mm, "end": v(-1240.19, 280) * mm});
            skLineSegment(sketch, "E93", {"start": v(-1240.19, 280) * mm, "end": v(-1320.19, 280) * mm});
            skLineSegment(sketch, "E94", {"start": v(-280.19, 320) * mm, "end": v(-280.19, 280) * mm});
            skPoint(sketch, "E94.startSnap0", {"position": v(-320.19, 320) * mm});
            skLineSegment(sketch, "E95", {"start": v(-280.19, 280) * mm, "end": v(-360.19, 280) * mm});
            skLineSegment(sketch, "E96", {"start": v(-360.19, 280) * mm, "end": v(-360.19, 320) * mm});
            skLineSegment(sketch, "E97", {"start": v(599.81, 280) * mm, "end": v(599.81, 320) * mm});
            skLineSegment(sketch, "E98", {"start": v(599.81, 280) * mm, "end": v(679.81, 280) * mm});
            skPoint(sketch, "E99.orphan", {"position": v(679.81, 320) * mm});
            skLineSegment(sketch, "E100.trimOffspring", {"start": v(-280.19, 320) * mm, "end": v(599.81, 320) * mm});
            skPoint(sketch, "E101.orphan", {"position": v(-1320.19, 320) * mm});
            skSolve(sketch);
        }
        {
            var Q0;
            Q0=makeQuery(id+"F51.imprint","IMPRINT",FACE,{"disambiguationData":[TD([[makeQuery(id+"F51.imprint","IMPRINT",EDGE,{"derivedFrom":sQuery(id+"F51.wireOp",EDGE,"E86.bottom")}),-1.0]])]});
            extrude(context, id + "F52", {"entities" : qUnion([Q0]), "depth" : 12 * mm, "offsetDistance" : 25 * mm});
        }
        {
            var Q0;
            Q0=qCreatedBy(makeId("Front.planeOp"),FACE);
            var sketch = newSketch(context, id + "F53", { "sketchPlane" : qUnion([Q0])});
            skLineSegment(sketch, "E102.bottom", {"start": v(-75.18, 52) * mm, "end": v(4.82, 52) * mm});
            skLineSegment(sketch, "E102.top", {"start": v(-75.18, 12) * mm, "end": v(4.82, 12) * mm});
            skLineSegment(sketch, "E102.left", {"start": v(-75.18, 52) * mm, "end": v(-75.18, 12) * mm});
            skLineSegment(sketch, "E102.right", {"start": v(4.82, 52) * mm, "end": v(4.82, 12) * mm});
            skSolve(sketch);
        }
        {
            var Q0;
            Q0=makeQuery(id+"F53.imprint","IMPRINT",FACE,{"disambiguationData":[TD([[makeQuery(id+"F53.imprint","IMPRINT",EDGE,{"derivedFrom":sQuery(id+"F53.wireOp",EDGE,"E102.bottom")}),-1.0]])]});
            extrude(context, id + "F54", {"entities" : qUnion([Q0]), "depth" : 430 * mm, "offsetDistance" : 25 * mm});
        }
        {
            var Q0;
            Q0=makeQuery(id+"F54.opExtrude","SWEPT_EDGE",EDGE,{"disambiguationData":[OSD([sQuery(id+"F53.wireOp",EDGE,"E102.bottom"),sQuery(id+"F53.wireOp",EDGE,"E102.left")])]});
            var Q1;
            Q1=makeQuery(id+"F54.opExtrude","SWEPT_EDGE",EDGE,{"disambiguationData":[OSD([sQuery(id+"F53.wireOp",EDGE,"E102.bottom"),sQuery(id+"F53.wireOp",EDGE,"E102.right")])]});
            var Q2;
            Q2=makeQuery(id+"F54.opExtrude","SWEPT_EDGE",EDGE,{"disambiguationData":[OSD([sQuery(id+"F53.wireOp",EDGE,"E102.top"),sQuery(id+"F53.wireOp",EDGE,"E102.right")])]});
            var Q3;
            Q3=makeQuery(id+"F54.opExtrude","SWEPT_EDGE",EDGE,{"disambiguationData":[OSD([sQuery(id+"F53.wireOp",EDGE,"E102.top"),sQuery(id+"F53.wireOp",EDGE,"E102.left")])]});
            fillet(context, id + "F55", {"entities" : qUnion([Q0, Q1, Q2, Q3]), "radius" : 5 * mm, "tangentPropagation" : true, "allowEdgeOverflow" : false});
        }
        {
            var Q0;
            Q0=makeQuery(id+"F54.opExtrude","CAP_FACE",FACE,{"disambiguationData":[OSD([sQuery(id+"F53.wireOp",EDGE,"E102.bottom"),sQuery(id+"F53.wireOp",EDGE,"E102.top"),sQuery(id+"F53.wireOp",EDGE,"E102.left"),sQuery(id+"F53.wireOp",EDGE,"E102.right")])],"isStart":false});
            var sketch = newSketch(context, id + "F56", { "sketchPlane" : qUnion([Q0])});
            skPoint(sketch, "E103", {"position": v(-55.18, 32) * mm});
            skPoint(sketch, "E103.positionSnap0", {"position": v(-75.18, 32) * mm});
            skPoint(sketch, "E104", {"position": v(-15.18, 32) * mm});
            skSolve(sketch);
        }
        {
            var Q0;
            Q0=sQuery(id+"F56.wireOp",VERTEX,"E103");
            var Q1;
            Q1=sQuery(id+"F56.wireOp",VERTEX,"E104");
            var Q2;
            Q2=makeQuery(id+"F54.opExtrude","SWEPT_BODY",BODY,{"disambiguationData":[OSD([sQuery(id+"F53.wireOp",EDGE,"E102.bottom"),sQuery(id+"F53.wireOp",EDGE,"E102.top"),sQuery(id+"F53.wireOp",EDGE,"E102.left"),sQuery(id+"F53.wireOp",EDGE,"E102.right")])]});
            hole(context, id + "F57", {"style" : HoleStyle.SIMPLE, "endStyle" : HoleEndStyle.THROUGH, "holeDiameter" : 6 * mm, "majorDiameter" : 5 * mm, "isTappedThrough" : true, "tappedDepth" : 12 * mm, "tapClearance" : 3, "locations" : qUnion([Q0, Q1]), "scope" : qUnion([Q2])});
        }
        {
            var Q0;
            Q0=qCreatedBy(makeId("Front.planeOp"),FACE);
            var sketch = newSketch(context, id + "F58", { "sketchPlane" : qUnion([Q0])});
            skLineSegment(sketch, "E105.bottom", {"start": v(-35.76, 33.8) * mm, "end": v(-5.76, 33.8) * mm});
            skLineSegment(sketch, "E105.top", {"start": v(-45.76, 23.8) * mm, "end": v(-5.76, 23.8) * mm});
            skLineSegment(sketch, "E105.right", {"start": v(-5.76, 33.8) * mm, "end": v(-5.76, 23.8) * mm});
            skArc(sketch, "E106", {"start": v(-35.76, 33.8) * mm, "mid": v(-52.83, 40.87) * mm, "end": v(-45.76, 23.8) * mm});
            skSolve(sketch);
        }
        {
            var Q0;
            Q0=makeQuery(id+"F58.imprint","IMPRINT",FACE,{"disambiguationData":[TD([[makeQuery(id+"F58.imprint","IMPRINT",EDGE,{"derivedFrom":sQuery(id+"F58.wireOp",EDGE,"E105.bottom")}),-1.0]])]});
            extrude(context, id + "F59", {"entities" : qUnion([Q0]), "depth" : 40 * mm, "offsetDistance" : 25 * mm});
        }
        {
            var Q0;
            Q0=makeQuery(id+"F59.opExtrude","CAP_FACE",FACE,{"disambiguationData":[OSD([sQuery(id+"F58.wireOp",EDGE,"E105.bottom"),sQuery(id+"F58.wireOp",EDGE,"E105.top"),sQuery(id+"F58.wireOp",EDGE,"E105.right"),sQuery(id+"F58.wireOp",EDGE,"E106")])],"isStart":false});
            var sketch = newSketch(context, id + "F60", { "sketchPlane" : qUnion([Q0])});
            skPoint(sketch, "E107", {"position": v(-45.76, 33.8) * mm});
            skSolve(sketch);
        }
        {
            var Q0;
            Q0=makeQuery(id+"F59.opExtrude","SWEPT_FACE",FACE,{"disambiguationData":[OSD([sQuery(id+"F58.wireOp",EDGE,"E105.bottom")])]});
            var sketch = newSketch(context, id + "F61", { "sketchPlane" : qUnion([Q0])});
            skPoint(sketch, "E108", {"position": v(-25.76, -20) * mm});
            skPoint(sketch, "E108.positionSnap0", {"position": v(-5.76, -20) * mm});
            skSolve(sketch);
        }
        {
            var Q0;
            Q0=sQuery(id+"F61.wireOp",VERTEX,"E108");
            var Q1;
            Q1=sQuery(id+"F60.wireOp",VERTEX,"E107");
            var Q2;
            Q2=makeQuery(id+"F59.opExtrude","SWEPT_BODY",BODY,{"disambiguationData":[OSD([sQuery(id+"F58.wireOp",EDGE,"E105.bottom"),sQuery(id+"F58.wireOp",EDGE,"E105.top"),sQuery(id+"F58.wireOp",EDGE,"E105.right"),sQuery(id+"F58.wireOp",EDGE,"E106")])]});
            hole(context, id + "F62", {"style" : HoleStyle.SIMPLE, "endStyle" : HoleEndStyle.THROUGH, "holeDiameter" : 6 * mm, "majorDiameter" : 5 * mm, "isTappedThrough" : true, "tappedDepth" : 12 * mm, "tapClearance" : 3, "locations" : qUnion([Q0, Q1]), "scope" : qUnion([Q2])});
        }
        {
            var Q0;
            Q0=makeQuery(id+"F59.opExtrude","CAP_EDGE",EDGE,{"disambiguationData":[OSD([sQuery(id+"F58.wireOp",EDGE,"E105.bottom")])],"isStart":false});
            var Q1;
            Q1=makeQuery(id+"F59.opExtrude","SWEPT_EDGE",EDGE,{"disambiguationData":[OSD([sQuery(id+"F58.wireOp",EDGE,"E105.bottom"),sQuery(id+"F58.wireOp",EDGE,"E105.right")])]});
            var Q2;
            Q2=makeQuery(id+"F59.opExtrude","CAP_EDGE",EDGE,{"disambiguationData":[OSD([sQuery(id+"F58.wireOp",EDGE,"E105.bottom")])],"isStart":true});
            var Q3;
            Q3=makeQuery(id+"F59.opExtrude","CAP_EDGE",EDGE,{"disambiguationData":[OSD([sQuery(id+"F58.wireOp",EDGE,"E105.top")])],"isStart":false});
            var Q4;
            Q4=makeQuery(id+"F59.opExtrude","SWEPT_EDGE",EDGE,{"disambiguationData":[OSD([sQuery(id+"F58.wireOp",EDGE,"E105.top"),sQuery(id+"F58.wireOp",EDGE,"E105.right")])]});
            var Q5;
            Q5=makeQuery(id+"F59.opExtrude","CAP_EDGE",EDGE,{"disambiguationData":[OSD([sQuery(id+"F58.wireOp",EDGE,"E105.top")])],"isStart":true});
            var Q6;
            Q6=makeQuery(id+"F59.opExtrude","CAP_EDGE",EDGE,{"disambiguationData":[OSD([sQuery(id+"F58.wireOp",EDGE,"E105.right")])],"isStart":false});
            var Q7;
            Q7=makeQuery(id+"F59.opExtrude","CAP_EDGE",EDGE,{"disambiguationData":[OSD([sQuery(id+"F58.wireOp",EDGE,"E105.right")])],"isStart":true});
            fillet(context, id + "F63", {"entities" : qUnion([Q0, Q1, Q2, Q3, Q4, Q5, Q6, Q7]), "radius" : 2 * mm, "tangentPropagation" : true, "allowEdgeOverflow" : false});
        }
        {
            var Q0;
            Q0=qCreatedBy(makeId("Front.planeOp"),FACE);
            var sketch = newSketch(context, id + "F64", { "sketchPlane" : qUnion([Q0])});
            skLineSegment(sketch, "E109.bottom", {"start": v(22.67, -22.67) * mm, "end": v(52.67, -22.67) * mm});
            skLineSegment(sketch, "E109.top", {"start": v(12.67, -32.67) * mm, "end": v(52.67, -32.67) * mm});
            skLineSegment(sketch, "E109.right", {"start": v(52.67, -22.67) * mm, "end": v(52.67, -32.67) * mm});
            skArc(sketch, "E110", {"start": v(12.67, -32.67) * mm, "mid": v(19.74, -29.74) * mm, "end": v(22.67, -22.67) * mm});
            skSolve(sketch);
        }
        {
            var Q0;
            Q0=makeQuery(id+"F64.imprint","IMPRINT",FACE,{"disambiguationData":[TD([[makeQuery(id+"F64.imprint","IMPRINT",EDGE,{"derivedFrom":sQuery(id+"F64.wireOp",EDGE,"E109.bottom")}),-1.0]])]});
            extrude(context, id + "F65", {"entities" : qUnion([Q0]), "depth" : 40 * mm, "offsetDistance" : 25 * mm});
        }
        {
            var Q0;
            Q0=makeQuery(id+"F65.opExtrude","CAP_EDGE",EDGE,{"disambiguationData":[OSD([sQuery(id+"F64.wireOp",EDGE,"E109.bottom")])],"isStart":false});
            var Q1;
            Q1=makeQuery(id+"F65.opExtrude","CAP_EDGE",EDGE,{"disambiguationData":[OSD([sQuery(id+"F64.wireOp",EDGE,"E109.bottom")])],"isStart":true});
            var Q2;
            Q2=makeQuery(id+"F65.opExtrude","SWEPT_EDGE",EDGE,{"disambiguationData":[OSD([sQuery(id+"F64.wireOp",EDGE,"E109.bottom"),sQuery(id+"F64.wireOp",EDGE,"E109.right")])]});
            var Q3;
            Q3=makeQuery(id+"F65.opExtrude","CAP_EDGE",EDGE,{"disambiguationData":[OSD([sQuery(id+"F64.wireOp",EDGE,"E109.right")])],"isStart":true});
            var Q4;
            Q4=makeQuery(id+"F65.opExtrude","CAP_EDGE",EDGE,{"disambiguationData":[OSD([sQuery(id+"F64.wireOp",EDGE,"E109.right")])],"isStart":false});
            var Q5;
            Q5=makeQuery(id+"F65.opExtrude","CAP_EDGE",EDGE,{"disambiguationData":[OSD([sQuery(id+"F64.wireOp",EDGE,"E109.top")])],"isStart":false});
            var Q6;
            Q6=makeQuery(id+"F65.opExtrude","SWEPT_EDGE",EDGE,{"disambiguationData":[OSD([sQuery(id+"F64.wireOp",EDGE,"E109.top"),sQuery(id+"F64.wireOp",EDGE,"E109.right")])]});
            var Q7;
            Q7=makeQuery(id+"F65.opExtrude","CAP_EDGE",EDGE,{"disambiguationData":[OSD([sQuery(id+"F64.wireOp",EDGE,"E109.top")])],"isStart":true});
            fillet(context, id + "F66", {"entities" : qUnion([Q0, Q1, Q2, Q3, Q4, Q5, Q6, Q7]), "radius" : 2 * mm, "tangentPropagation" : true, "allowEdgeOverflow" : false});
        }
        {
            var Q0;
            Q0=makeQuery(id+"F65.opExtrude","SWEPT_FACE",FACE,{"disambiguationData":[OSD([sQuery(id+"F64.wireOp",EDGE,"E109.bottom")])]});
            var sketch = newSketch(context, id + "F67", { "sketchPlane" : qUnion([Q0])});
            skPoint(sketch, "E111", {"position": v(30.67, -20) * mm});
            skPoint(sketch, "E111.positionSnap0", {"position": v(50.67, -20) * mm});
            skSolve(sketch);
        }
        {
            var Q0;
            Q0=sQuery(id+"F67.wireOp",VERTEX,"E111");
            var Q1;
            Q1=makeQuery(id+"F65.opExtrude","SWEPT_BODY",BODY,{"disambiguationData":[OSD([sQuery(id+"F64.wireOp",EDGE,"E109.bottom"),sQuery(id+"F64.wireOp",EDGE,"E109.top"),sQuery(id+"F64.wireOp",EDGE,"E109.right"),sQuery(id+"F64.wireOp",EDGE,"E110")])]});
            hole(context, id + "F68", {"style" : HoleStyle.SIMPLE, "endStyle" : HoleEndStyle.THROUGH, "holeDiameter" : 6 * mm, "majorDiameter" : 5 * mm, "isTappedThrough" : true, "tappedDepth" : 12 * mm, "tapClearance" : 3, "locations" : qUnion([Q0]), "scope" : qUnion([Q1])});
        }
        {
            var Q0;
            Q0=qCreatedBy(makeId("Front.planeOp"),FACE);
            var sketch = newSketch(context, id + "F69", { "sketchPlane" : qUnion([Q0])});
            skLineSegment(sketch, "E112.bottom", {"start": v(-71.33, 39.27) * mm, "end": v(8.67, 39.27) * mm});
            skLineSegment(sketch, "E112.top", {"start": v(-71.33, -0.73) * mm, "end": v(8.67, -0.73) * mm});
            skLineSegment(sketch, "E112.left", {"start": v(-71.33, 39.27) * mm, "end": v(-71.33, -0.73) * mm});
            skLineSegment(sketch, "E112.right", {"start": v(8.67, 39.27) * mm, "end": v(8.67, -0.73) * mm});
            skSolve(sketch);
        }
        {
            var Q0;
            Q0=makeQuery(id+"F69.imprint","IMPRINT",FACE,{"disambiguationData":[TD([[makeQuery(id+"F69.imprint","IMPRINT",EDGE,{"derivedFrom":sQuery(id+"F69.wireOp",EDGE,"E112.bottom")}),-1.0]])]});
            extrude(context, id + "F70", {"entities" : qUnion([Q0]), "depth" : 91 * mm, "offsetDistance" : 25 * mm});
        }
        {
            var Q0;
            Q0=makeQuery(id+"F70.opExtrude","SWEPT_EDGE",EDGE,{"disambiguationData":[OSD([sQuery(id+"F69.wireOp",EDGE,"E112.bottom"),sQuery(id+"F69.wireOp",EDGE,"E112.left")])]});
            var Q1;
            Q1=makeQuery(id+"F70.opExtrude","SWEPT_EDGE",EDGE,{"disambiguationData":[OSD([sQuery(id+"F69.wireOp",EDGE,"E112.bottom"),sQuery(id+"F69.wireOp",EDGE,"E112.right")])]});
            var Q2;
            Q2=makeQuery(id+"F70.opExtrude","SWEPT_EDGE",EDGE,{"disambiguationData":[OSD([sQuery(id+"F69.wireOp",EDGE,"E112.top"),sQuery(id+"F69.wireOp",EDGE,"E112.right")])]});
            var Q3;
            Q3=makeQuery(id+"F70.opExtrude","SWEPT_EDGE",EDGE,{"disambiguationData":[OSD([sQuery(id+"F69.wireOp",EDGE,"E112.top"),sQuery(id+"F69.wireOp",EDGE,"E112.left")])]});
            fillet(context, id + "F71", {"entities" : qUnion([Q0, Q1, Q2, Q3]), "radius" : 5 * mm, "tangentPropagation" : true, "allowEdgeOverflow" : false});
        }
        {
            var Q0;
            Q0=makeQuery(id+"F70.opExtrude","CAP_FACE",FACE,{"disambiguationData":[OSD([sQuery(id+"F69.wireOp",EDGE,"E112.bottom"),sQuery(id+"F69.wireOp",EDGE,"E112.top"),sQuery(id+"F69.wireOp",EDGE,"E112.left"),sQuery(id+"F69.wireOp",EDGE,"E112.right")])],"isStart":false});
            var sketch = newSketch(context, id + "F72", { "sketchPlane" : qUnion([Q0])});
            skPoint(sketch, "E113", {"position": v(-51.33, 19.27) * mm});
            skPoint(sketch, "E113.positionSnap0", {"position": v(-71.33, 19.27) * mm});
            skPoint(sketch, "E114", {"position": v(-11.33, 19.27) * mm});
            skSolve(sketch);
        }
        {
            var Q0;
            Q0=sQuery(id+"F72.wireOp",VERTEX,"E113");
            var Q1;
            Q1=sQuery(id+"F72.wireOp",VERTEX,"E114");
            var Q2;
            Q2=makeQuery(id+"F70.opExtrude","SWEPT_BODY",BODY,{"disambiguationData":[OSD([sQuery(id+"F69.wireOp",EDGE,"E112.bottom"),sQuery(id+"F69.wireOp",EDGE,"E112.top"),sQuery(id+"F69.wireOp",EDGE,"E112.left"),sQuery(id+"F69.wireOp",EDGE,"E112.right")])]});
            hole(context, id + "F73", {"style" : HoleStyle.SIMPLE, "endStyle" : HoleEndStyle.THROUGH, "holeDiameter" : 6 * mm, "majorDiameter" : 5 * mm, "isTappedThrough" : true, "tappedDepth" : 12 * mm, "tapClearance" : 3, "locations" : qUnion([Q0, Q1]), "scope" : qUnion([Q2])});
        }
    });
